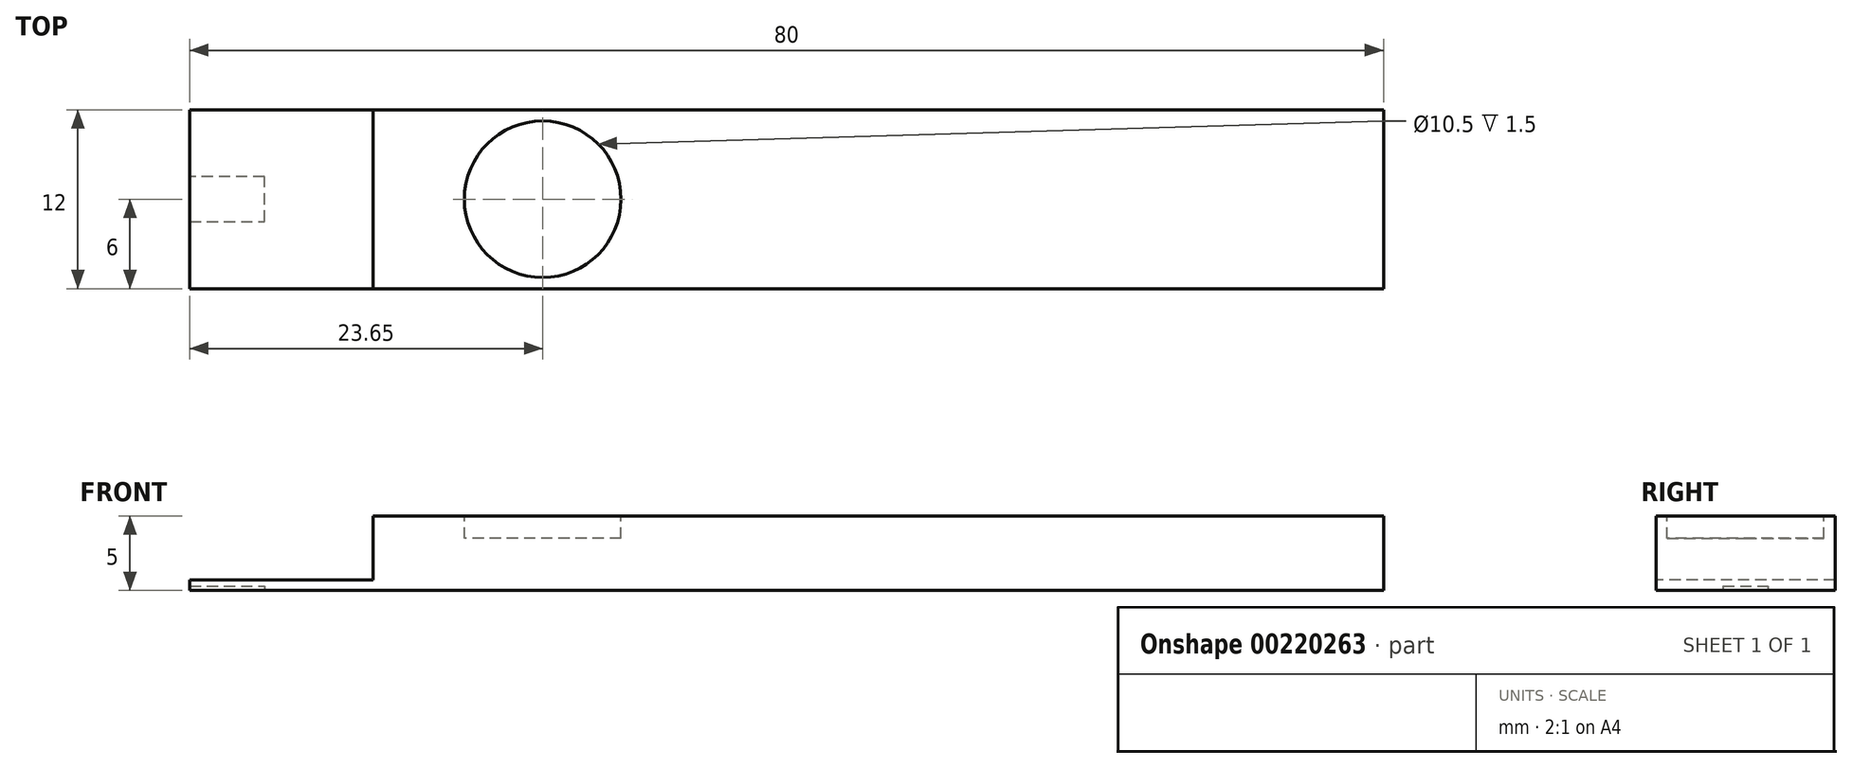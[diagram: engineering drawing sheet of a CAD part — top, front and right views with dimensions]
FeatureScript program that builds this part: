
annotation { "Feature Type Name" : "Feature", "Feature Type Description" : "" }
export const myFeature = defineFeature(function(context is Context, id is Id, definition is map)
    precondition{}
    {
        {
            var Q0;
            Q0=qCreatedBy(makeId("Top.planeOp"),FACE);
            var sketch = newSketch(context, id + "F0", { "sketchPlane" : qUnion([Q0])});
            skLineSegment(sketch, "E0.bottom", {"start": v(40, 6) * mm, "end": v(-40, 6) * mm});
            skLineSegment(sketch, "E0.top", {"start": v(40, -6) * mm, "end": v(-40, -6) * mm});
            skLineSegment(sketch, "E0.left", {"start": v(40, 6) * mm, "end": v(40, -6) * mm});
            skLineSegment(sketch, "E0.right", {"start": v(-40, 6) * mm, "end": v(-40, -6) * mm});
            skPoint(sketch, "E0.middle", {"position": v(0, 0) * mm});
            skLineSegment(sketch, "E1", {"start": v(0, 0) * mm, "end": v(-40, 0) * mm});
            skLineSegment(sketch, "E2", {"start": v(-27.7, 6) * mm, "end": v(-27.7, -6) * mm});
            skSolve(sketch);
        }
        {
            var Q0;
            {var subQ0=sQuery(id+"F0.wireOp",EDGE,"E0.right");var subQ1=sQuery(id+"F0.wireOp",EDGE,"E0.top");var subQ2=makeQuery(id+"F0.imprint","INTERSECT",VERTEX,{"derivedFrom":[subQ1,subQ0]});Q0=makeQuery(id+"F0.imprint","IMPRINT",FACE,{"disambiguationData":[TD([[makeQuery(id+"F0.imprint","IMPRINT",EDGE,{"disambiguationData":[TD([[subQ2,1.0]])],"derivedFrom":subQ1}),-1.0]])]});}
            var Q1;
            {var subQ0=sQuery(id+"F0.wireOp",EDGE,"E0.right");var subQ1=sQuery(id+"F0.wireOp",EDGE,"E0.bottom");var subQ2=makeQuery(id+"F0.imprint","INTERSECT",VERTEX,{"derivedFrom":[subQ1,subQ0]});Q1=makeQuery(id+"F0.imprint","IMPRINT",FACE,{"disambiguationData":[TD([[makeQuery(id+"F0.imprint","IMPRINT",EDGE,{"disambiguationData":[TD([[subQ2,1.0]])],"derivedFrom":subQ1}),1.0]])]});}
            extrude(context, id + "F1", {"entities" : qUnion([Q0, Q1]), "depth" : 0.7 * mm});
        }
        {
            var Q0;
            Q0=qCreatedBy(makeId("Top.planeOp"),FACE);
            var sketch = newSketch(context, id + "F2", { "sketchPlane" : qUnion([Q0])});
            skLineSegment(sketch, "E3", {"start": v(-40, -1.5) * mm, "end": v(-35, -1.5) * mm});
            skLineSegment(sketch, "E4", {"start": v(-35, -1.5) * mm, "end": v(-35, 1.5) * mm});
            skLineSegment(sketch, "E5", {"start": v(-35, 1.5) * mm, "end": v(-40, 1.5) * mm});
            skLineSegment(sketch, "E6", {"start": v(-40, -1.5) * mm, "end": v(-40, 1.5) * mm});
            skSolve(sketch);
        }
        {
            var Q0;
            {var subQ4=sQuery(id+"F0.wireOp",EDGE,"E0.left");Q0=makeQuery(id+"F0.imprint","IMPRINT",FACE,{"disambiguationData":[TD([[makeQuery(id+"F0.imprint","IMPRINT",EDGE,{"derivedFrom":subQ4}),-1.0]])]});}
            extrude(context, id + "F3", {"entities" : qUnion([Q0]), "operationType" : NewBodyOperationType.ADD, "depth" : 5 * mm});
        }
        {
            var Q0;
            Q0=makeQuery(id+"F3.opExtrude","CAP_FACE",FACE,{"disambiguationData":[OSD([sQuery(id+"F0.wireOp",EDGE,"E0.bottom"),sQuery(id+"F0.wireOp",EDGE,"E0.top"),sQuery(id+"F0.wireOp",EDGE,"E0.left"),sQuery(id+"F0.wireOp",EDGE,"E0.right")])],"isStart":false});
            var sketch = newSketch(context, id + "F4", { "sketchPlane" : qUnion([Q0])});
            skCircle(sketch, "E7", {"center": v(-16.35, 0) * mm, "radius": 5.25 * mm});
            skSolve(sketch);
        }
        {
            var Q0;
            Q0=makeQuery(id+"F4.imprint","IMPRINT",FACE,{"disambiguationData":[TD([[makeQuery(id+"F4.imprint","IMPRINT",EDGE,{"derivedFrom":sQuery(id+"F4.wireOp",EDGE,"E7")}),1.0]])]});
            var Q1;
            Q1=sQuery(id+"F4.wireOp",EDGE,"E7");
            extrude(context, id + "F5", {"entities" : qUnion([Q0]), "operationType" : NewBodyOperationType.REMOVE, "surfaceEntities" : qUnion([Q1]), "oppositeDirection" : true, "depth" : 1.5 * mm});
        }
        {
            var Q0;
            Q0=makeQuery(id+"F2.imprint","IMPRINT",FACE,{"disambiguationData":[TD([[makeQuery(id+"F2.imprint","IMPRINT",EDGE,{"derivedFrom":sQuery(id+"F2.wireOp",EDGE,"E3")}),1.0]])]});
            extrude(context, id + "F6", {"entities" : qUnion([Q0]), "operationType" : NewBodyOperationType.REMOVE, "depth" : 0.3 * mm});
        }
    });
